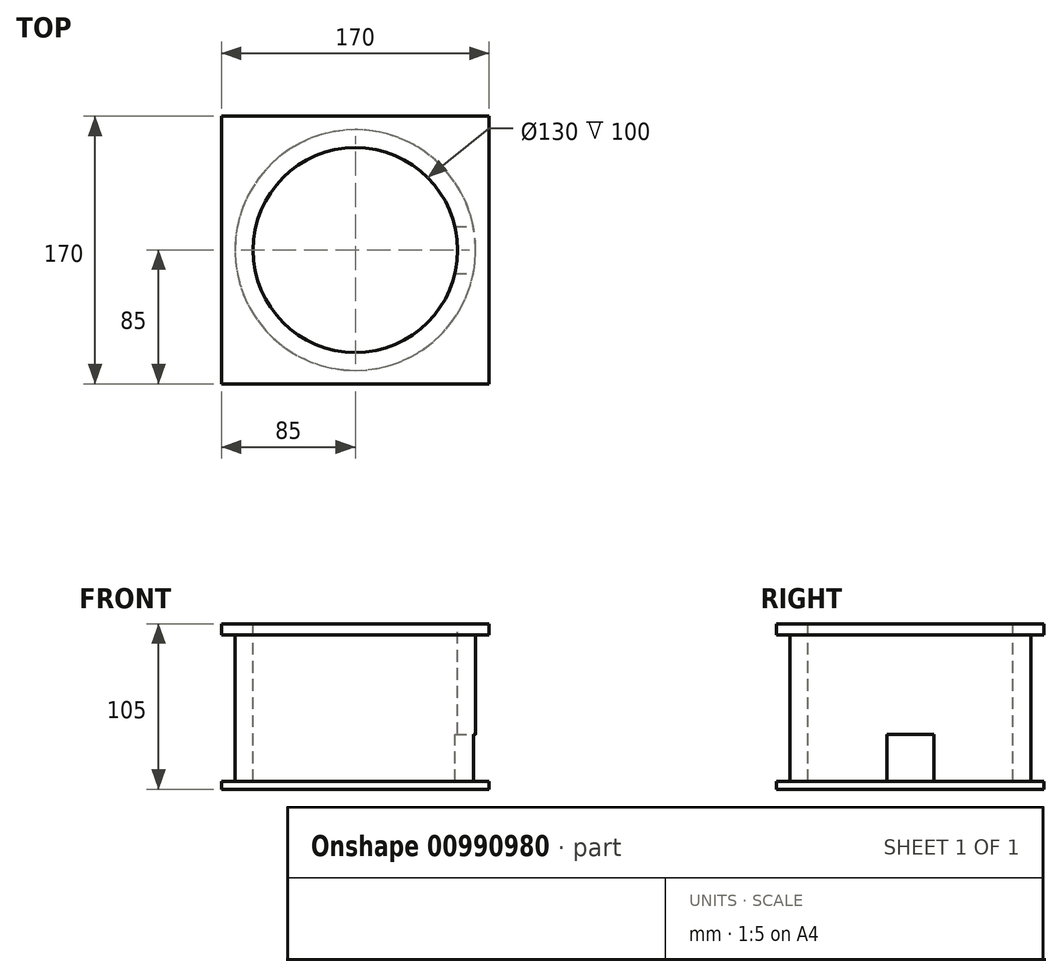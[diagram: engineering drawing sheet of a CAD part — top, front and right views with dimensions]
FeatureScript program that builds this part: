
annotation { "Feature Type Name" : "Feature", "Feature Type Description" : "" }
export const myFeature = defineFeature(function(context is Context, id is Id, definition is map)
    precondition{}
    {
        {
            var Q0;
            Q0=qCreatedBy(makeId("Top.planeOp"),FACE);
            var sketch = newSketch(context, id + "F0", { "sketchPlane" : qUnion([Q0])});
            skCircle(sketch, "E0", {"center": v(0, 0) * mm, "radius": 65 * mm});
            skLineSegment(sketch, "E1.bottom", {"start": v(85, -85) * mm, "end": v(-85, -85) * mm});
            skLineSegment(sketch, "E1.top", {"start": v(85, 85) * mm, "end": v(-85, 85) * mm});
            skLineSegment(sketch, "E1.left", {"start": v(85, -85) * mm, "end": v(85, 85) * mm});
            skLineSegment(sketch, "E1.right", {"start": v(-85, -85) * mm, "end": v(-85, 85) * mm});
            skPoint(sketch, "E2", {"position": v(-85, 0) * mm});
            skPoint(sketch, "E3", {"position": v(85, 0) * mm});
            skPoint(sketch, "E4", {"position": v(0, 85) * mm});
            skPoint(sketch, "E5", {"position": v(0, -85) * mm});
            skCircle(sketch, "E6", {"center": v(0, 0) * mm, "radius": 76.43 * mm});
            skSolve(sketch);
        }
        {
            var Q0;
            Q0=makeQuery(id+"F0.imprint","IMPRINT",FACE,{"disambiguationData":[TD([[makeQuery(id+"F0.imprint","IMPRINT",EDGE,{"derivedFrom":sQuery(id+"F0.wireOp",EDGE,"E0")}),-1.0]])]});
            extrude(context, id + "F1", {"entities" : qUnion([Q0]), "oppositeDirection" : true, "depth" : 100 * mm, "offsetDistance" : 25 * mm});
        }
        {
            var Q0;
            Q0=qSketchRegion(id+"F0",true);
            extrude(context, id + "F2", {"entities" : qUnion([Q0]), "operationType" : NewBodyOperationType.ADD, "oppositeDirection" : true, "depth" : 7 * mm, "offsetDistance" : 25 * mm});
        }
        {
            var Q0;
            Q0=makeQuery(id+"F1.opExtrude","CAP_FACE",FACE,{"disambiguationData":[OSD([sQuery(id+"F0.wireOp",EDGE,"E0"),sQuery(id+"F0.wireOp",EDGE,"E1.bottom"),sQuery(id+"F0.wireOp",EDGE,"E1.top"),sQuery(id+"F0.wireOp",EDGE,"E1.left"),sQuery(id+"F0.wireOp",EDGE,"E1.right"),sQuery(id+"F0.wireOp",EDGE,"E6")])],"isStart":false});
            var sketch = newSketch(context, id + "F3", { "sketchPlane" : qUnion([Q0])});
            skLineSegment(sketch, "E7.bottom", {"start": v(85, -85) * mm, "end": v(-85, -85) * mm});
            skLineSegment(sketch, "E7.top", {"start": v(85, 85) * mm, "end": v(-85, 85) * mm});
            skLineSegment(sketch, "E7.left", {"start": v(85, -85) * mm, "end": v(85, 85) * mm});
            skLineSegment(sketch, "E7.right", {"start": v(-85, -85) * mm, "end": v(-85, 85) * mm});
            skPoint(sketch, "E7.middle", {"position": v(0, 0) * mm});
            skSolve(sketch);
        }
        {
            var Q0;
            Q0 = qSketchRegion(id + "F3", true);
            extrude(context, id + "F4", {"entities" : qUnion([Q0]), "operationType" : NewBodyOperationType.ADD, "depth" : 5 * mm, "offsetDistance" : 25 * mm});
        }
        {
            var Q0;
            Q0=makeQuery(id+"F4.opExtrude","SWEPT_FACE",FACE,{"disambiguationData":[OSD([sQuery(id+"F3.wireOp",EDGE,"E7.left")])]});
            var sketch = newSketch(context, id + "F5", { "sketchPlane" : qUnion([Q0])});
            skLineSegment(sketch, "E8", {"start": v(0, -100) * mm, "end": v(0, -36.5) * mm, "construction": true});
            skLineSegment(sketch, "E9", {"start": v(15, -100) * mm, "end": v(15, -70) * mm});
            skLineSegment(sketch, "E10", {"start": v(15, -70) * mm, "end": v(0, -70) * mm});
            skLineSegment(sketch, "E11.MirrorCS", {"start": v(-15, -70) * mm, "end": v(0, -70) * mm});
            skLineSegment(sketch, "E12.MirrorCS", {"start": v(-15, -100) * mm, "end": v(-15, -70) * mm});
            skSolve(sketch);
        }
        {
            var Q0;
            {var subQ1=sQuery(id+"F5.wireOp",EDGE,"E9");Q0=makeQuery(id+"F5.imprint","IMPRINT",FACE,{"disambiguationData":[TD([[makeQuery(id+"F5.imprint","IMPRINT",EDGE,{"derivedFrom":subQ1}),1.0]])]});}
            var Q1;
            Q1=makeQuery(id+"F1.opExtrude","SWEPT_FACE",FACE,{"disambiguationData":[OSD([sQuery(id+"F0.wireOp",EDGE,"E0")])]});
            extrude(context, id + "F6", {"entities" : qUnion([Q0]), "operationType" : NewBodyOperationType.REMOVE, "endBound" : BoundingType.UP_TO_SURFACE, "oppositeDirection" : true, "depth" : 25 * mm, "endBoundEntityFace" : qUnion([Q1]), "offsetDistance" : 25 * mm});
        }
    });
